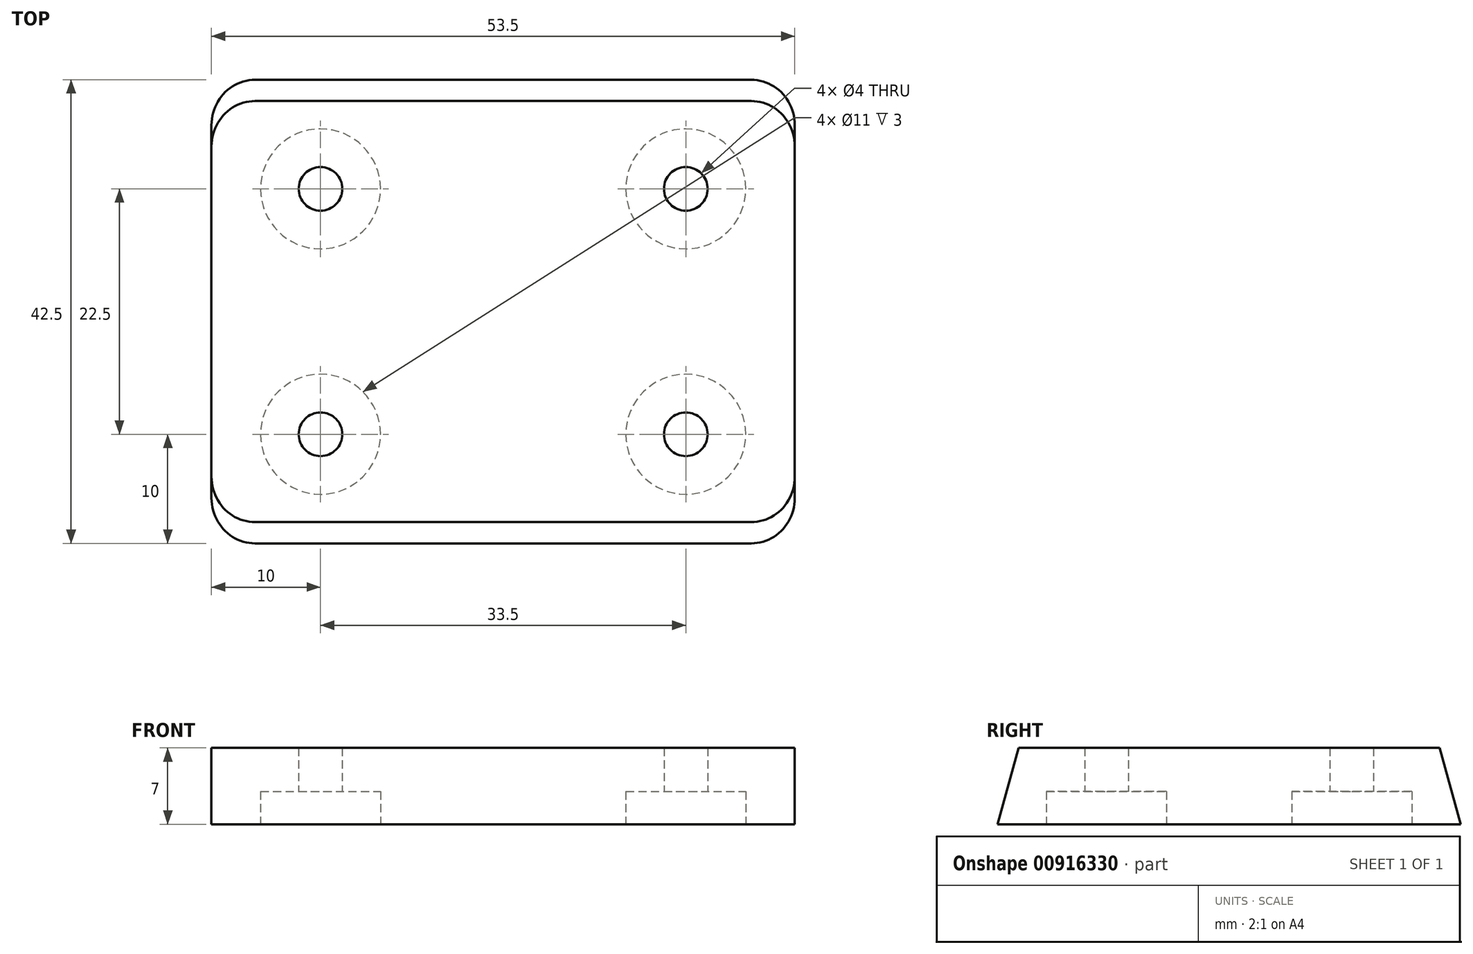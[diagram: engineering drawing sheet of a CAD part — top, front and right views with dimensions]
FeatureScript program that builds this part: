
annotation { "Feature Type Name" : "Feature", "Feature Type Description" : "" }
export const myFeature = defineFeature(function(context is Context, id is Id, definition is map)
    precondition{}
    {
        {
            assignVariable(context, id + "F0", {"name" : "base_width", "anyValue" : 53.5});
        }
        {
            var Q0;
            Q0=qCreatedBy(makeId("Right.planeOp"),FACE);
            var sketch = newSketch(context, id + "F1", { "sketchPlane" : qUnion([Q0])});
            skLineSegment(sketch, "E0", {"start": v(-21.25, 0) * mm, "end": v(21.25, 0) * mm});
            skLineSegment(sketch, "E1", {"start": v(21.25, 0) * mm, "end": v(19.3, 7) * mm});
            skLineSegment(sketch, "E2", {"start": v(19.3, 7) * mm, "end": v(-19.3, 7) * mm});
            skLineSegment(sketch, "E3", {"start": v(-19.3, 7) * mm, "end": v(-21.25, 0) * mm});
            skLineSegment(sketch, "E4", {"start": v(0, 0) * mm, "end": v(0, 7) * mm, "construction": true});
            skSolve(sketch);
        }
        {
            var Q0;
            Q0=makeQuery(id+"F1.imprint","IMPRINT",FACE,{"disambiguationData":[TD([[makeQuery(id+"F1.imprint","IMPRINT",EDGE,{"derivedFrom":sQuery(id+"F1.wireOp",EDGE,"E0")}),1.0]])]});
            extrude(context, id + "F2", {"entities" : qUnion([Q0]), "depth" : (getVariable(context, 'base_width')) * mm, "symmetric" : true});
        }
        {
            var Q0;
            Q0=makeQuery(id+"F2.opExtrude","CAP_EDGE",EDGE,{"disambiguationData":[OSD([sQuery(id+"F1.wireOp",EDGE,"E3")])],"isStart":true});
            var Q1;
            Q1=makeQuery(id+"F2.opExtrude","CAP_EDGE",EDGE,{"disambiguationData":[OSD([sQuery(id+"F1.wireOp",EDGE,"E3")])],"isStart":false});
            var Q2;
            Q2=makeQuery(id+"F2.opExtrude","CAP_EDGE",EDGE,{"disambiguationData":[OSD([sQuery(id+"F1.wireOp",EDGE,"E1")])],"isStart":false});
            var Q3;
            Q3=makeQuery(id+"F2.opExtrude","CAP_EDGE",EDGE,{"disambiguationData":[OSD([sQuery(id+"F1.wireOp",EDGE,"E1")])],"isStart":true});
            fillet(context, id + "F3", {"entities" : qUnion([Q0, Q1, Q2, Q3]), "radius" : 4 * mm, "tangentPropagation" : true, "allowEdgeOverflow" : false});
        }
        {
            var Q0;
            Q0=makeQuery(id+"F2.opExtrude","SWEPT_FACE",FACE,{"disambiguationData":[OSD([sQuery(id+"F1.wireOp",EDGE,"E0")])]});
            var sketch = newSketch(context, id + "F4", { "sketchPlane" : qUnion([Q0])});
            skPoint(sketch, "E5", {"position": v(16.75, 11.25) * mm});
            skPoint(sketch, "E6.MirrorP", {"position": v(-16.75, 11.25) * mm});
            skPoint(sketch, "E7.MirrorP", {"position": v(16.75, -11.25) * mm});
            skPoint(sketch, "E8.MirrorP", {"position": v(-16.75, -11.25) * mm});
            skSolve(sketch);
        }
        {
            var Q0;
            Q0=sQuery(id+"F4.wireOp",VERTEX,"E6.MirrorP");
            var Q1;
            Q1=sQuery(id+"F4.wireOp",VERTEX,"E5");
            var Q2;
            Q2=sQuery(id+"F4.wireOp",VERTEX,"E7.MirrorP");
            var Q3;
            Q3=sQuery(id+"F4.wireOp",VERTEX,"E8.MirrorP");
            var Q4;
            Q4=makeQuery(id+"F2.opExtrude","SWEPT_BODY",BODY,{"disambiguationData":[OSD([sQuery(id+"F1.wireOp",EDGE,"E0"),sQuery(id+"F1.wireOp",EDGE,"E1"),sQuery(id+"F1.wireOp",EDGE,"E2"),sQuery(id+"F1.wireOp",EDGE,"E3")])]});
            hole(context, id + "F5", {"style" : HoleStyle.C_BORE, "endStyle" : HoleEndStyle.BLIND, "holeDiameter" : 4 * mm, "cBoreDiameter" : 11 * mm, "cBoreDepth" : 3 * mm, "majorDiameter" : 4 * mm, "holeDepth" : 14.1 * mm, "isTappedThrough" : true, "tappedDepth" : 12 * mm, "tapClearance" : 3, "locations" : qUnion([Q0, Q1, Q2, Q3]), "scope" : qUnion([Q4])});
        }
    });
